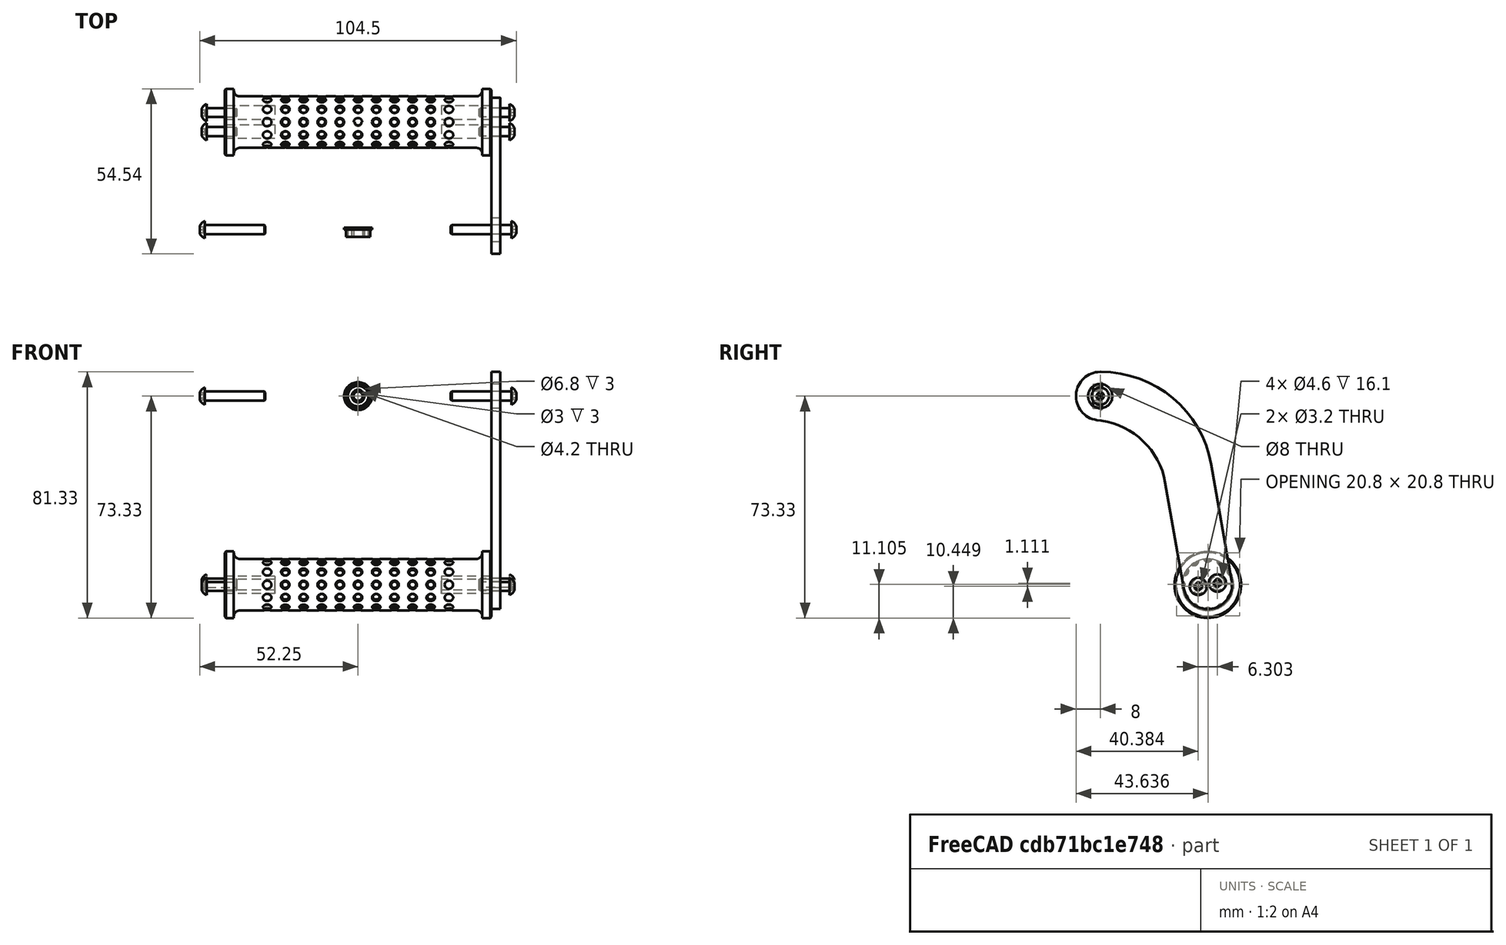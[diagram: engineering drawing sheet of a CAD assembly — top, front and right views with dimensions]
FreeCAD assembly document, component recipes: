
FREECAD ASSEMBLY — COMPONENT RECIPES ("handle")

This assembly document has 2 components, labeled P0..P1 below (a component is one placed body or linked part). 2 of them carry a construction recipe — the FreeCAD feature program that regenerates the part from scratch, quoted from this document or its linked companion documents; the rest are supplied as boundary geometry only. No exploded tour is included for this assembly.
COMPONENT P0 — recipe-attached ("Handle", modeled in this document).
Construction recipe (the document's own serialized feature program — sketch geometry with constraints, then the solid features built on it; lengths are millimeters unless a unit is written):

FEATURE [PartDesign::SubShapeBinder] Binder001  label="Binder001(Fillet012)"
  BindCopyOnChange = 0
  BindMode = 2
  ClaimChildren = false
  Context = -> <external ../holonomic-base.FCStd>#Link002 [Part015.Part017.Body025.Binder001.]
  EdgeTolerance = 1e-06
  FillStyle = 0
  FixShape = 1
  Fuse = false
  InvalidShape = false
  MakeFace = true
  MergeEdges = true
  OffsetFill = false
  OffsetIntersection = false
  OffsetJoinType = 0
  OffsetOpenResult = false
  Outline = false
  PartialLoad = false
  Relative = true
  SplitEdges = false
  TightBound = false
  TreeRank = 235
  ValidateShape = false
  _Version = 8
FEATURE [PartDesign::Plane] DatumPlane002
  AttachmentOffset = pos=(0,0,0) rot=(0,1,0;1.5708rad)
  FixShape = 1
  InvalidShape = false
  Length = 88
  MapMode = 45
  MinimumLength = 10
  MinimumWidth = 10
  Placement = pos=(1.95e-14,35.5351,-62.3257) rot=(0,0.707107,0.707107;3.14159rad)
  ResizeMode = 0
  TreeRank = 118
  ValidateShape = false
  Width = 22
FEATURE [Sketcher::SketchObject] Sketch
  ArcFitTolerance = 1e-06
  AttachmentSupport = -> [YZ_Plane041]
  ExternalBSplineMaxDegree = 5
  ExternalBSplineTolerance = 0.0001
  FixShape = 1
  FullyConstrained = true
  InternalTolerance = 1e-06
  InvalidShape = false
  MakeInternals = false
  MapMode = 5
  Placement = pos=(0,0,0) rot=(0.57735,0.57735,0.57735;2.0944rad)
  Support = -> [YZ_Plane041]
  TreeRank = 44
  ValidateShape = false
  sketch-geometry (14):
    g0: ArcOfCircle CenterX=0 CenterY=0 CenterZ=0 NormalX=0 NormalY=0 NormalZ=1 AngleXU=0 Radius=8 StartAngle=1.5708 EndAngle=4.57276
    g1: Circle CenterX=0 CenterY=0 CenterZ=0 NormalX=0 NormalY=0 NormalZ=1 AngleXU=0 Radius=4
    g2: LineSegment StartX=0 StartY=8 StartZ=0 EndX=31.2582 EndY=8 EndZ=0
    g3: LineSegment StartX=31.2582 StartY=8 StartZ=0 EndX=43.4136 EndY=-60.9365 EndZ=0
    g4: ArcOfCircle CenterX=35.5351 CenterY=-62.3257 CenterZ=0 NormalX=0 NormalY=0 NormalZ=1 AngleXU=0 Radius=8 StartAngle=3.31613 EndAngle=6.45772
    g5: LineSegment StartX=27.6567 StartY=-63.7149 StartZ=0 EndX=18.3 EndY=-10.6505 EndZ=0
    g6: LineSegment StartX=-1.11338 StartY=-7.92214 StartZ=0 EndX=18.3 EndY=-10.6505 EndZ=0
    g7: LineSegment [constr] StartX=24.6104 StartY=-63.7149 StartZ=0 EndX=15.2537 EndY=-10.6505 EndZ=0
    g8: LineSegment [constr] StartX=27.6567 StartY=-63.7149 StartZ=0 EndX=43.4136 EndY=-60.9365 EndZ=0
    g9: Circle CenterX=32.3838 CenterY=-62.8814 CenterZ=0 NormalX=0 NormalY=0 NormalZ=1 AngleXU=0 Radius=1.6
    g10: Circle CenterX=38.6865 CenterY=-61.7701 CenterZ=0 NormalX=0 NormalY=0 NormalZ=1 AngleXU=0 Radius=1.6
    g11: LineSegment [constr] StartX=27.6567 StartY=-63.7149 StartZ=0 EndX=30.8081 EndY=-63.1592 EndZ=0
    g12: LineSegment [constr] StartX=33.9595 StartY=-62.6036 StartZ=0 EndX=37.1108 EndY=-62.0479 EndZ=0
    g13: LineSegment [constr] StartX=40.2622 StartY=-61.4922 StartZ=0 EndX=43.4136 EndY=-60.9365 EndZ=0
  constraints (41):
    c: Coincident(g0,g-1)
    c: PointOnObject(g0,g-2)
    c: Coincident(g1,g0)
    c: Diameter(g1) = 8
    c: DistanceY(g0,g0) = 8
    c: Coincident(g2,g0)
    c: Horizontal(g2)
    c: Coincident(g3,g2)
    c: Angle(g2,g3) = 1.74533
    c: Tangent(g4,g3) = 1.5708
    c: Coincident(g6,g5)
    c: Tangent(g6,g0) = -1.5708
    c: Parallel(g5,g3)
    c: Parallel(g7,g5)
    c: Distance(g7,g5) = 3
    c: Equal(g0,g4)
    c: Angle(g6,g5) = 1.88496
    c: DistanceX(g0,g5) = 18.3
    c: Tangent(g5,g4) = 1.5708
    c: Distance(g3) = 70
    c: Coincident(g8,g4)
    c: Coincident(g8,g3)
    c: PointOnObject(g9,g8)
    c: Equal(g10,g9)
    c: Diameter(g10) = 3.2
    c: Symmetric(g9,g10,g4)
    c: Coincident(g11,g4)
    c: PointOnObject(g11,g8)
    c: PointOnObject(g12,g8)
    c: PointOnObject(g12,g8)
    c: PointOnObject(g13,g8)
    c: Coincident(g13,g3)
    c: PointOnObject(g13,g10)
    c: PointOnObject(g12,g10)
    c: PointOnObject(g12,g9)
    c: PointOnObject(g11,g9)
    c: Equal(g11,g12)
    c: Horizontal(g7,g5)
    c: Horizontal(g4,g7)
    c: DistanceX(g4) = 35.5351
    c: DistanceY(g4) = -62.3257
FEATURE [PartDesign::Pad] Pad
  AddSubType = 0
  AlongSketchNormal = false
  AutoTaperInnerAngle = true
  CheckUpToFaceLimits = true
  ClaimChildren = false
  Direction = (1,-2e-16,3e-16)
  Fit = 0
  FitJoin = 0
  FixShape = 1
  InnerFit = 0
  InnerFitJoin = 0
  InvalidShape = false
  Length = 3
  Length2 = 10
  Linearize = true
  NewSolid = false
  Profile = -> Sketch
  ReferenceAxis = -> Sketch [N_Axis]
  Refine = true
  Suppress = false
  TaperInnerAngle = 0
  TaperInnerAngleRev = 0
  TreeRank = 45
  Type = 0
  ValidateShape = true
  _ProfileBasedVersion = 1
FEATURE [PartDesign::Fillet] Fillet
  AddSubType = 0
  Base = -> Pad [Edge8]
  BaseFeature = -> Pad
  FixShape = 1
  InvalidShape = false
  NewSolid = false
  Radius = 25
  Refine = true
  SupportTransform = false
  Suppress = false
  TreeRank = 46
  UseAllEdges = false
  ValidateShape = true
FEATURE [PartDesign::Fillet] Fillet012
  AddSubType = 0
  Base = -> Fillet [Edge26]
  BaseFeature = -> Fillet
  FixShape = 1
  InvalidShape = false
  NewSolid = false
  Radius = 37
  Refine = true
  SupportTransform = false
  Suppress = false
  TreeRank = 47
  UseAllEdges = false
  ValidateShape = true
FEATURE [PartDesign::Body] Body  label="HandlePlate"
  AutoGroupSolids = false
  ClaimAllChildren = false
  ExportMode = 0
  FixShape = 1
  Group = -> [Sketch,Pad,Fillet,Fillet012]
  InvalidShape = false
  Origin = -> Origin055
  Placement = pos=(44,0,0) rot=(0,0,1;0rad)
  SingleSolid = true
  Tip = -> Fillet012
  TreeRank = 236
  ValidateShape = false
  _ExportChildren = -> [Pad,Fillet,Fillet012]
  _GroupVersion = 1
FEATURE [Sketcher::SketchObject] Sketch045
  ArcFitTolerance = 1e-06
  AttachmentSupport = -> [YZ_Plane045]
  ExternalBSplineMaxDegree = 5
  ExternalBSplineTolerance = 0.0001
  ExternalGeometry = -> [Binder001]
  FixShape = 1
  FullyConstrained = true
  InternalTolerance = 1e-06
  InvalidShape = false
  MakeInternals = false
  MapMode = 5
  Placement = pos=(0,0,0) rot=(0.57735,0.57735,0.57735;2.0944rad)
  Support = -> [YZ_Plane045]
  TreeRank = 115
  ValidateShape = false
  sketch-geometry (4):
    g0: Circle [constr] CenterX=35.5351 CenterY=-62.3257 CenterZ=0 NormalX=0 NormalY=0 NormalZ=1 AngleXU=0 Radius=6
    g1: Circle CenterX=35.5351 CenterY=-62.3257 CenterZ=0 NormalX=0 NormalY=0 NormalZ=1 AngleXU=0 Radius=8.5
    g2: Circle CenterX=32.3838 CenterY=-62.8814 CenterZ=0 NormalX=0 NormalY=0 NormalZ=1 AngleXU=0 Radius=2.3
    g3: Circle CenterX=38.6865 CenterY=-61.7701 CenterZ=0 NormalX=0 NormalY=0 NormalZ=1 AngleXU=0 Radius=2.3
  constraints (8):
    c: Coincident(g0,g-3)
    c: Diameter(g0) = 12
    c: Coincident(g1,g0)
    c: Diameter(g1) = 17
    c: Coincident(g2,g-4)
    c: Coincident(g3,g-5)
    c: Equal(g3,g2)
    c: Diameter(g3) = 4.6
FEATURE [PartDesign::Pad] Pad026
  AddSubType = 0
  AlongSketchNormal = false
  AutoTaperInnerAngle = true
  CheckUpToFaceLimits = true
  ClaimChildren = false
  Direction = (1,-2e-16,3e-16)
  Fit = 0
  FitJoin = 0
  FixShape = 1
  InnerFit = 0
  InnerFitJoin = 0
  InvalidShape = false
  Length = 88
  Length2 = 10
  Linearize = true
  Midplane = true
  NewSolid = false
  Profile = -> Sketch045
  ReferenceAxis = -> Sketch045 [N_Axis]
  Refine = true
  Suppress = false
  TaperInnerAngle = 0
  TaperInnerAngleRev = 0
  TreeRank = 116
  Type = 0
  ValidateShape = true
  _ProfileBasedVersion = 1
FEATURE [Sketcher::SketchObject] Sketch046
  ArcFitTolerance = 1e-06
  AttachmentSupport = -> [DatumPlane002]
  ExternalBSplineMaxDegree = 5
  ExternalBSplineTolerance = 0.0001
  ExternalGeometry = -> [Pad026]
  FixShape = 1
  FullyConstrained = true
  InternalTolerance = 1e-06
  InvalidShape = false
  MakeInternals = false
  MapMode = 5
  Placement = pos=(1.95e-14,35.5351,-62.3257) rot=(0,0.707107,0.707107;3.14159rad)
  Support = -> [DatumPlane002]
  TreeRank = 119
  ValidateShape = false
  sketch-geometry (8):
    g0: LineSegment StartX=-44 StartY=8.5 StartZ=0 EndX=-41 EndY=8.5 EndZ=0
    g1: LineSegment StartX=-41 StartY=8.5 StartZ=0 EndX=-41 EndY=11 EndZ=0
    g2: LineSegment StartX=-41 StartY=11 StartZ=0 EndX=-44 EndY=11 EndZ=0
    g3: LineSegment StartX=-44 StartY=11 StartZ=0 EndX=-44 EndY=8.5 EndZ=0
    g4: LineSegment StartX=44 StartY=8.5 StartZ=0 EndX=41 EndY=8.5 EndZ=0
    g5: LineSegment StartX=41 StartY=8.5 StartZ=0 EndX=41 EndY=11 EndZ=0
    g6: LineSegment StartX=41 StartY=11 StartZ=0 EndX=44 EndY=11 EndZ=0
    g7: LineSegment StartX=44 StartY=11 StartZ=0 EndX=44 EndY=8.5 EndZ=0
  constraints (22):
    c: Coincident(g0,g1)
    c: Coincident(g1,g2)
    c: Coincident(g2,g3)
    c: Coincident(g3,g0)
    c: Horizontal(g0)
    c: Horizontal(g2)
    c: Vertical(g1)
    c: Vertical(g3)
    c: Coincident(g4,g5)
    c: Coincident(g5,g6)
    c: Coincident(g6,g7)
    c: Coincident(g7,g4)
    c: Horizontal(g4)
    c: Horizontal(g6)
    c: Vertical(g5)
    c: Vertical(g7)
    c: Symmetric(g4,g0,g-2)
    c: Equal(g0,g4)
    c: Equal(g5,g1)
    c: DistanceX(g2,g2) = 3
    c: DistanceY(g-1,g2) = 11
    c: Coincident(g0,g-3)
FEATURE [PartDesign::Revolution] Revolution
  AddSubType = 0
  Angle = 360
  Axis = (-1,1e-16,-1e-16)
  Base = (1.95e-14,35.5351,-62.3257)
  BaseFeature = -> Pad026
  ClaimChildren = false
  Fit = 0
  FitJoin = 0
  FixShape = 1
  InnerFit = 0
  InnerFitJoin = 0
  InvalidShape = false
  Linearize = true
  NewSolid = false
  Profile = -> Sketch046
  ReferenceAxis = -> Sketch046 [H_Axis]
  Refine = true
  Suppress = false
  TreeRank = 120
  ValidateShape = true
  _ProfileBasedVersion = 1
FEATURE [PartDesign::Chamfer] Chamfer008
  AddSubType = 0
  Angle = 45
  Base = -> Revolution [Edge11,Edge9,Edge17,Edge15,Edge13,Edge12]
  BaseFeature = -> Revolution
  ChamferType = 0
  FixShape = 1
  FlipDirection = false
  InvalidShape = false
  NewSolid = false
  Refine = true
  Size = 0.4
  Size2 = 1
  SupportTransform = false
  Suppress = false
  TreeRank = 121
  UseAllEdges = false
  ValidateShape = true
FEATURE [PartDesign::Fillet] Fillet014
  AddSubType = 0
  Base = -> Chamfer008 [Edge7,Edge11]
  BaseFeature = -> Chamfer008
  FixShape = 1
  InvalidShape = false
  NewSolid = false
  Radius = 2
  Refine = true
  SupportTransform = false
  Suppress = false
  TreeRank = 122
  UseAllEdges = false
  ValidateShape = true
FEATURE [Sketcher::SketchObject] Sketch047
  ArcFitTolerance = 1e-06
  AttachmentSupport = -> [DatumPlane002]
  ExternalBSplineMaxDegree = 5
  ExternalBSplineTolerance = 0.0001
  FixShape = 1
  FullyConstrained = true
  InternalTolerance = 1e-06
  InvalidShape = false
  MakeInternals = false
  MapMode = 5
  Placement = pos=(1.95e-14,35.5351,-62.3257) rot=(0,0.707107,0.707107;3.14159rad)
  Support = -> [DatumPlane002]
  TreeRank = 143
  ValidateShape = false
  sketch-geometry (2):
    g0: ArcOfCircle CenterX=0 CenterY=9 CenterZ=0 NormalX=0 NormalY=0 NormalZ=1 AngleXU=0 Radius=1.5 StartAngle=1.5708 EndAngle=4.71239
    g1: LineSegment StartX=0 StartY=10.5 StartZ=0 EndX=0 EndY=7.5 EndZ=0
  constraints (7):
    c: PointOnObject(g0,g-2)
    c: PointOnObject(g0,g-2)
    c: Coincident(g1,g0)
    c: Coincident(g1,g0)
    c: Vertical(g1)
    c: DistanceY(g-1,g0) = 9
    c: Radius(g0) = 1.5
FEATURE [PartDesign::Groove] Groove001
  AddSubType = 1
  Angle = 360
  Axis = (-1e-16,-2e-16,1)
  Base = (1.95e-14,35.5351,-62.3257)
  BaseFeature = -> Fillet014
  ClaimChildren = false
  Fit = 0
  FitJoin = 0
  FixShape = 1
  InnerFit = 0
  InnerFitJoin = 0
  InvalidShape = false
  Linearize = true
  NewSolid = false
  Profile = -> Sketch047
  ReferenceAxis = -> Sketch047 [V_Axis]
  Refine = true
  Reversed = true
  Suppress = false
  TreeRank = 144
  ValidateShape = true
  _ProfileBasedVersion = 1
FEATURE [PartDesign::Line] DatumLine001
  AttacherType = Attacher::AttachEngineLine
  AttachmentSupport = -> [Groove001]
  FixShape = 1
  InvalidShape = false
  Length = 10
  MapMode = 44
  MinimumLength = 10
  Placement = pos=(-2.90702e-10,35.5351,-62.3382) rot=(0.57735,0.57735,0.57735;2.0944rad)
  ResizeMode = 0
  Support = -> [Groove001]
  TreeRank = 145
  ValidateShape = false
FEATURE [PartDesign::LinearPattern] LinearPattern
  AddSubType = 0
  CopyShape = false
  Direction = -> Sketch047 [H_Axis]
  FixShape = 1
  HideBaseFeature = false
  InvalidShape = false
  Length = 30
  NewSolid = false
  Occurrences = 6
  OffsetBaseFeature = true
  ParallelTransform = true
  Refine = true
  SubTransform = true
  Suppress = false
  TreeRank = 148
  ValidateShape = true
  _Version = 3
FEATURE [PartDesign::Mirrored] Mirrored
  AddSubType = 0
  CopyShape = false
  FixShape = 1
  HideBaseFeature = false
  InvalidShape = false
  MirrorPlane = -> Sketch047 [V_Axis]
  NewSolid = false
  OffsetBaseFeature = true
  ParallelTransform = true
  Refine = true
  SubTransform = true
  Suppress = false
  TreeRank = 149
  ValidateShape = true
  _Version = 3
FEATURE [PartDesign::PolarPattern] PolarPattern014
  AddSubType = 0
  Angle = 360
  Axis = -> DatumLine001
  CopyShape = false
  FixShape = 1
  HideBaseFeature = false
  InvalidShape = false
  NewSolid = false
  Occurrences = 12
  OffsetBaseFeature = true
  ParallelTransform = true
  Refine = true
  SubTransform = true
  Suppress = false
  TreeRank = 147
  ValidateShape = true
  _Version = 3
FEATURE [PartDesign::MultiTransform] MultiTransform
  AddSubType = 0
  BaseFeature = -> Groove001
  CopyShape = false
  FixShape = 1
  HideBaseFeature = false
  InvalidShape = false
  NewSolid = false
  OffsetBaseFeature = true
  OriginalSubs = -> [Groove001]
  Originals = -> [Groove001]
  ParallelTransform = true
  Refine = true
  SubTransform = true
  Suppress = false
  Transformations = -> [PolarPattern014,LinearPattern,Mirrored]
  TreeRank = 146
  ValidateShape = true
  _Version = 3
FEATURE [Sketcher::SketchObject] Sketch056
  ArcFitTolerance = 1e-06
  AttachmentSupport = -> [YZ_Plane045]
  ExternalBSplineMaxDegree = 5
  ExternalBSplineTolerance = 0.0001
  ExternalGeometry = -> [Binder001]
  FixShape = 1
  FullyConstrained = true
  InternalTolerance = 1e-06
  InvalidShape = false
  MakeInternals = false
  MapMode = 5
  Placement = pos=(0,0,0) rot=(0.57735,0.57735,0.57735;2.0944rad)
  Support = -> [YZ_Plane045]
  TreeRank = 232
  ValidateShape = false
  sketch-geometry (1):
    g0: Circle CenterX=35.5351 CenterY=-62.3257 CenterZ=0 NormalX=0 NormalY=0 NormalZ=1 AngleXU=0 Radius=8
  constraints (2):
    c: Coincident(g0,g-3)
    c: PointOnObject(g-3,g0)
FEATURE [PartDesign::Pad] Pad031
  AddSubType = 0
  AlongSketchNormal = false
  AutoTaperInnerAngle = true
  BaseFeature = -> MultiTransform
  CheckUpToFaceLimits = true
  ClaimChildren = false
  Direction = (1,-2e-16,3e-16)
  Fit = 0
  FitJoin = 0
  FixShape = 1
  InnerFit = 0
  InnerFitJoin = 0
  InvalidShape = false
  Length = 55
  Length2 = 10
  Linearize = true
  Midplane = true
  NewSolid = false
  Profile = -> Sketch056
  ReferenceAxis = -> Sketch056 [N_Axis]
  Refine = true
  Suppress = false
  TaperInnerAngle = 0
  TaperInnerAngleRev = 0
  TreeRank = 233
  Type = 0
  ValidateShape = true
  _ProfileBasedVersion = 1
FEATURE [PartDesign::Body] Body025  label="TexturedHandle"
  AutoGroupSolids = false
  ClaimAllChildren = false
  ExportMode = 0
  FixShape = 1
  Group = -> [Binder001,Sketch045,Pad026,DatumPlane002,Sketch046,Revolution,Chamfer008,Fillet014,Sketch047,Groove001,DatumLine001,MultiTransform,PolarPattern014,LinearPattern,Mirrored,Sketch056,Pad031]
  InvalidShape = false
  Origin = -> Origin059
  SingleSolid = true
  Tip = -> Pad031
  TreeRank = 238
  ValidateShape = false
  _ExportChildren = -> [Binder001,Pad026,DatumPlane002,Revolution,Chamfer008,Fillet014,Groove001,DatumLine001,MultiTransform,Pad031]
  _GroupVersion = 1
COMPONENT P1 — recipe-attached ("MF83", modeled in this document).
Construction recipe (the document's own serialized feature program — sketch geometry with constraints, then the solid features built on it; lengths are millimeters unless a unit is written):

FEATURE [Sketcher::SketchObject] Sketch160
  ArcFitTolerance = 0
  ExternalBSplineMaxDegree = 0
  ExternalBSplineTolerance = 0
  FixShape = 1
  FullyConstrained = true
  InternalTolerance = 1e-06
  InvalidShape = false
  MakeInternals = false
  MapMode = 5
  TreeRank = 253
  ValidateShape = false
  sketch-geometry (10):
    g0: LineSegment StartX=-4.6 StartY=0 StartZ=0 EndX=-4.6 EndY=0.6 EndZ=0
    g1: LineSegment StartX=-4.6 StartY=0.6 StartZ=0 EndX=-3.4 EndY=0.6 EndZ=0
    g2: LineSegment StartX=-3.4 StartY=0.6 StartZ=0 EndX=-3.4 EndY=-2.4 EndZ=0
    g3: LineSegment StartX=-3.4 StartY=-2.4 StartZ=0 EndX=-4 EndY=-2.4 EndZ=0
    g4: LineSegment StartX=-4 StartY=-2.4 StartZ=0 EndX=-4 EndY=0 EndZ=0
    g5: LineSegment StartX=-4 StartY=0 StartZ=0 EndX=-4.6 EndY=0 EndZ=0
    g6: LineSegment StartX=-2.1 StartY=0.6 StartZ=0 EndX=-1.5 EndY=0.6 EndZ=0
    g7: LineSegment StartX=-1.5 StartY=0.6 StartZ=0 EndX=-1.5 EndY=-2.4 EndZ=0
    g8: LineSegment StartX=-1.5 StartY=-2.4 StartZ=0 EndX=-2.1 EndY=-2.4 EndZ=0
    g9: LineSegment StartX=-2.1 StartY=-2.4 StartZ=0 EndX=-2.1 EndY=0.6 EndZ=0
  constraints (30):
    c: Vertical(g0)
    c: Coincident(g0,g1)
    c: Horizontal(g1)
    c: Coincident(g1,g2)
    c: Vertical(g2)
    c: Coincident(g2,g3)
    c: Horizontal(g3)
    c: Coincident(g3,g4)
    c: Vertical(g4)
    c: Coincident(g4,g5)
    c: Coincident(g5,g0)
    c: Horizontal(g5)
    c: Coincident(g6,g7)
    c: Coincident(g7,g8)
    c: Coincident(g8,g9)
    c: Coincident(g9,g6)
    c: Horizontal(g6)
    c: Horizontal(g8)
    c: Vertical(g7)
    c: Vertical(g9)
    c: PointOnObject(g6,g1)
    c: PointOnObject(g4,g-1)
    c: DistanceY(g2,g2) = 3
    c: PointOnObject(g8,g3)
    c: DistanceX(g3) = -4
    c: DistanceX(g6) = -1.5
    c: Equal(g3,g6)
    c: DistanceX(g6,g6) = 0.6
    c: DistanceX(g0) = -4.6
    c: DistanceY(g0,g0) = 0.6
FEATURE [PartDesign::Revolution] Revolution010
  AddSubType = 0
  Angle = 360
  Axis = (0,1,0)
  Base = (0,0,0)
  ClaimChildren = false
  Fit = 0
  FitJoin = 0
  FixShape = 1
  InnerFit = 0
  InnerFitJoin = 0
  InvalidShape = false
  NewSolid = false
  Profile = -> Sketch160
  ReferenceAxis = -> Sketch160 [V_Axis]
  Refine = true
  Suppress = false
  TreeRank = 0
  ValidateShape = true
  _ProfileBasedVersion = 0
FEATURE [PartDesign::Body] Body074  label="CoreMF83"
  AutoGroupSolids = false
  ClaimAllChildren = false
  ExportMode = 0
  FixShape = 1
  Group = -> [Sketch160,Revolution010]
  InvalidShape = false
  Origin = -> Origin158
  Placement = pos=(0,2.8e-14,0) rot=(0,0,1;0rad)
  Tip = -> Revolution010
  TreeRank = 0
  ValidateShape = false
  _ExportChildren = -> [Revolution010]
  _GroupVersion = 1
FEATURE [Sketcher::SketchObject] Sketch161
  ArcFitTolerance = 0
  ExternalBSplineMaxDegree = 0
  ExternalBSplineTolerance = 0
  FixShape = 1
  FullyConstrained = true
  InternalTolerance = 1e-06
  InvalidShape = false
  MakeInternals = false
  MapMode = 5
  TreeRank = 260
  ValidateShape = false
  sketch-geometry (4):
    g0: LineSegment StartX=-3.4 StartY=0.5 StartZ=0 EndX=-2.1 EndY=0.5 EndZ=0
    g1: LineSegment StartX=-2.1 StartY=0.5 StartZ=0 EndX=-2.1 EndY=-2.3 EndZ=0
    g2: LineSegment StartX=-2.1 StartY=-2.3 StartZ=0 EndX=-3.4 EndY=-2.3 EndZ=0
    g3: LineSegment StartX=-3.4 StartY=-2.3 StartZ=0 EndX=-3.4 EndY=0.5 EndZ=0
  constraints (12):
    c: Coincident(g0,g1)
    c: Coincident(g1,g2)
    c: Coincident(g2,g3)
    c: Coincident(g3,g0)
    c: Horizontal(g0)
    c: Horizontal(g2)
    c: Vertical(g1)
    c: Vertical(g3)
    c: DistanceY(g3,g3) = 2.8
    c: DistanceX(g0,g0) = 1.3
    c: DistanceX(g0,g-1) = 2.1
    c: DistanceY(g-1,g0) = 0.5
FEATURE [PartDesign::Revolution] Revolution011
  AddSubType = 0
  Angle = 360
  Axis = (1e-16,1,-1e-16)
  Base = (0,0,0)
  ClaimChildren = false
  Fit = 0
  FitJoin = 0
  FixShape = 1
  InnerFit = 0
  InnerFitJoin = 0
  InvalidShape = false
  NewSolid = false
  Profile = -> Sketch161
  ReferenceAxis = -> Y_Axis092
  Refine = true
  Suppress = false
  TreeRank = 0
  ValidateShape = true
  _ProfileBasedVersion = 0
FEATURE [PartDesign::Body] Body075  label="SleeveMF83"
  AutoGroupSolids = false
  ClaimAllChildren = false
  ExportMode = 0
  FixShape = 1
  Group = -> [Sketch161,Revolution011]
  InvalidShape = false
  Origin = -> Origin159
  Placement = pos=(0,2.8e-14,0) rot=(0,0,1;0rad)
  SingleSolid = true
  Tip = -> Revolution011
  TreeRank = 0
  ValidateShape = false
  _ExportChildren = -> [Revolution011]
  _GroupVersion = 1
PROVENANCE & LICENSES
A FreeCAD (.FCStd) document from a public repository crawl; recipes are the document's own serialized feature recipes (and, for linked parts, companion documents' recipes).
License: as declared in the source repository (recorded in the dataset sidecar).
